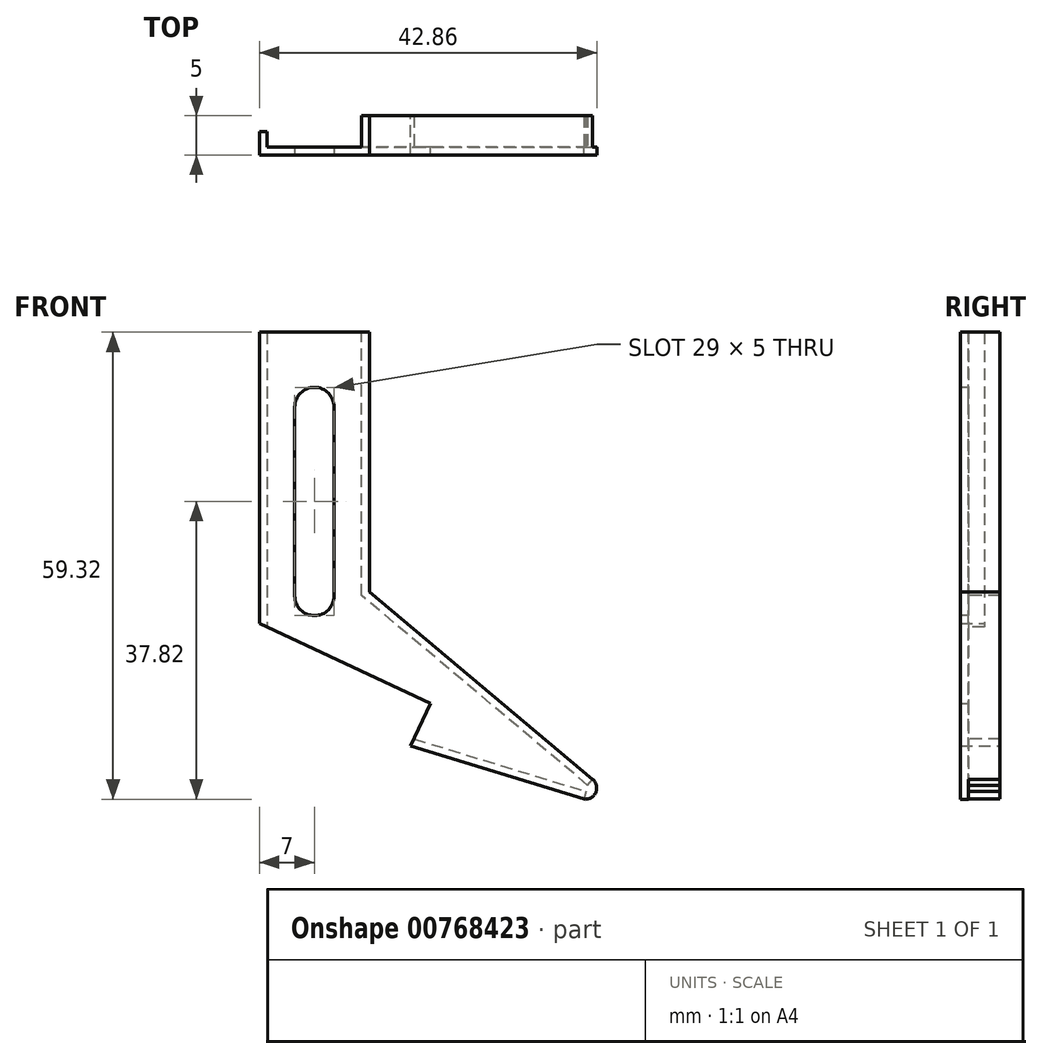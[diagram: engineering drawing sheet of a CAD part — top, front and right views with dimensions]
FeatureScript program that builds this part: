
annotation { "Feature Type Name" : "Feature", "Feature Type Description" : "" }
export const myFeature = defineFeature(function(context is Context, id is Id, definition is map)
    precondition{}
    {
        {
            var Q0;
            Q0=qCreatedBy(makeId("Front.planeOp"),FACE);
            var sketch = newSketch(context, id + "F0", { "sketchPlane" : qUnion([Q0])});
            skLineSegment(sketch, "E0", {"start": v(7, 0) * mm, "end": v(-7, 0) * mm});
            skLineSegment(sketch, "E1", {"start": v(-7, 0) * mm, "end": v(-7, -37) * mm});
            skLineSegment(sketch, "E2", {"start": v(-7, -37) * mm, "end": v(14.75, -47.14) * mm});
            skLineSegment(sketch, "E3", {"start": v(14.75, -47.14) * mm, "end": v(12.22, -52.58) * mm});
            skLineSegment(sketch, "E4", {"start": v(35.34, -56.78) * mm, "end": v(7, -33) * mm});
            skLineSegment(sketch, "E5", {"start": v(7, -33) * mm, "end": v(7, 0) * mm});
            skLineSegment(sketch, "E6", {"start": v(0, 0) * mm, "end": v(0, -40.26) * mm, "construction": true});
            skLineSegment(sketch, "E7", {"start": v(12.22, -52.58) * mm, "end": v(34.21, -59.3) * mm});
            skLineSegment(sketch, "E8", {"start": v(35.34, -56.78) * mm, "end": v(34.21, -59.3) * mm, "construction": true});
            skArc(sketch, "E9", {"start": v(35.34, -56.78) * mm, "mid": v(35.73, -58.47) * mm, "end": v(34.21, -59.3) * mm});
            skSolve(sketch);
        }
        {
            var Q0;
            Q0=makeQuery(id+"F0.imprint","IMPRINT",FACE,{"disambiguationData":[TD([[makeQuery(id+"F0.imprint","IMPRINT",EDGE,{"derivedFrom":sQuery(id+"F0.wireOp",EDGE,"E0")}),1.0]])]});
            extrude(context, id + "F1", {"entities" : qUnion([Q0]), "depth" : 1 * mm, "offsetDistance" : 25 * mm});
        }
        {
            var Q0;
            Q0=makeQuery(id+"F1.opExtrude","CAP_FACE",FACE,{"disambiguationData":[OSD([sQuery(id+"F0.wireOp",EDGE,"E0"),sQuery(id+"F0.wireOp",EDGE,"E1"),sQuery(id+"F0.wireOp",EDGE,"E2"),sQuery(id+"F0.wireOp",EDGE,"E3"),sQuery(id+"F0.wireOp",EDGE,"DroS7rj0-2XMO-sVTO-O5rM-PZIk5wrwzh7c"),sQuery(id+"F0.wireOp",EDGE,"E4"),sQuery(id+"F0.wireOp",EDGE,"E5")])],"isStart":true});
            var sketch = newSketch(context, id + "F2", { "sketchPlane" : qUnion([Q0])});
            skLineSegment(sketch, "E10", {"start": v(7, 0) * mm, "end": v(6, 0) * mm});
            skLineSegment(sketch, "E11", {"start": v(6, 0) * mm, "end": v(6, -37.47) * mm});
            skLineSegment(sketch, "E12", {"start": v(6, -37.47) * mm, "end": v(7, -37) * mm});
            skLineSegment(sketch, "E13", {"start": v(7, -37) * mm, "end": v(7, 0) * mm});
            skSolve(sketch);
        }
        {
            var Q0;
            Q0=makeQuery(id+"F2.imprint","IMPRINT",FACE,{"disambiguationData":[TD([[makeQuery(id+"F2.imprint","IMPRINT",EDGE,{"derivedFrom":sQuery(id+"F2.wireOp",EDGE,"E10")}),-1.0]])]});
            extrude(context, id + "F3", {"entities" : qUnion([Q0]), "operationType" : NewBodyOperationType.ADD, "depth" : 2 * mm, "offsetDistance" : 25 * mm});
        }
        {
            var Q0;
            Q0=makeQuery(id+"F1.opExtrude","CAP_FACE",FACE,{"disambiguationData":[OSD([sQuery(id+"F0.wireOp",EDGE,"E0"),sQuery(id+"F0.wireOp",EDGE,"E1"),sQuery(id+"F0.wireOp",EDGE,"E2"),sQuery(id+"F0.wireOp",EDGE,"E3"),sQuery(id+"F0.wireOp",EDGE,"DroS7rj0-2XMO-sVTO-O5rM-PZIk5wrwzh7c"),sQuery(id+"F0.wireOp",EDGE,"E4"),sQuery(id+"F0.wireOp",EDGE,"E5")])],"isStart":true});
            var sketch = newSketch(context, id + "F4", { "sketchPlane" : qUnion([Q0])});
            skLineSegment(sketch, "E14.0", {"start": v(-6, -33.47) * mm, "end": v(-6, 0) * mm});
            skLineSegment(sketch, "E14.1", {"start": v(-34.7, -57.55) * mm, "end": v(-6, -33.47) * mm});
            skLineSegment(sketch, "E15", {"start": v(-7, 0) * mm, "end": v(-6, 0) * mm});
            skLineSegment(sketch, "E16", {"start": v(-35.34, -56.78) * mm, "end": v(-7, -33) * mm});
            skLineSegment(sketch, "E17", {"start": v(-7, -33) * mm, "end": v(-7, 0) * mm});
            skLineSegment(sketch, "E18.0", {"start": v(-12.64, -51.67) * mm, "end": v(-34.5, -58.35) * mm});
            skLineSegment(sketch, "E19", {"start": v(-34.7, -57.55) * mm, "end": v(-35.34, -56.78) * mm});
            skLineSegment(sketch, "E20", {"start": v(-34.5, -58.35) * mm, "end": v(-34.21, -59.3) * mm});
            skLineSegment(sketch, "E21", {"start": v(-34.21, -59.3) * mm, "end": v(-12.22, -52.58) * mm});
            skLineSegment(sketch, "E22", {"start": v(-12.22, -52.58) * mm, "end": v(-12.64, -51.67) * mm});
            skSolve(sketch);
        }
        {
            var Q0;
            Q0=makeQuery(id+"F4.imprint","IMPRINT",FACE,{"disambiguationData":[TD([[makeQuery(id+"F4.imprint","IMPRINT",EDGE,{"derivedFrom":sQuery(id+"F4.wireOp",EDGE,"E14.0")}),1.0]])]});
            var Q1;
            Q1=makeQuery(id+"F4.imprint","IMPRINT",FACE,{"disambiguationData":[TD([[makeQuery(id+"F4.imprint","IMPRINT",EDGE,{"derivedFrom":sQuery(id+"F4.wireOp",EDGE,"E18.0")}),1.0]])]});
            extrude(context, id + "F5", {"entities" : qUnion([Q0, Q1]), "operationType" : NewBodyOperationType.ADD, "depth" : 4 * mm, "offsetDistance" : 25 * mm});
        }
        {
            var Q0;
            Q0=makeQuery(id+"F1.opExtrude","CAP_FACE",FACE,{"disambiguationData":[OSD([sQuery(id+"F0.wireOp",EDGE,"E0"),sQuery(id+"F0.wireOp",EDGE,"E1"),sQuery(id+"F0.wireOp",EDGE,"E2"),sQuery(id+"F0.wireOp",EDGE,"E3"),sQuery(id+"F0.wireOp",EDGE,"DroS7rj0-2XMO-sVTO-O5rM-PZIk5wrwzh7c"),sQuery(id+"F0.wireOp",EDGE,"E4"),sQuery(id+"F0.wireOp",EDGE,"E5")])],"isStart":false});
            var sketch = newSketch(context, id + "F6", { "sketchPlane" : qUnion([Q0])});
            skLineSegment(sketch, "E23", {"start": v(0, -33.5) * mm, "end": v(0, -9.5) * mm, "construction": true});
            skLineSegment(sketch, "E24", {"start": v(-2.5, -9.5) * mm, "end": v(-2.5, -33.5) * mm});
            skLineSegment(sketch, "E25", {"start": v(2.5, -33.5) * mm, "end": v(2.5, -9.5) * mm});
            skArc(sketch, "E26", {"start": v(2.5, -33.5) * mm, "mid": v(0, -36) * mm, "end": v(-2.5, -33.5) * mm});
            skArc(sketch, "E27", {"start": v(-2.5, -9.5) * mm, "mid": v(0, -7) * mm, "end": v(2.5, -9.5) * mm});
            skSolve(sketch);
        }
        {
            var Q0;
            Q0=makeQuery(id+"F6.imprint","IMPRINT",FACE,{"disambiguationData":[TD([[makeQuery(id+"F6.imprint","IMPRINT",EDGE,{"derivedFrom":sQuery(id+"F6.wireOp",EDGE,"E24")}),1.0]])]});
            extrude(context, id + "F7", {"entities" : qUnion([Q0]), "operationType" : NewBodyOperationType.REMOVE, "oppositeDirection" : true, "depth" : 25 * mm, "offsetDistance" : 25 * mm});
        }
    });
